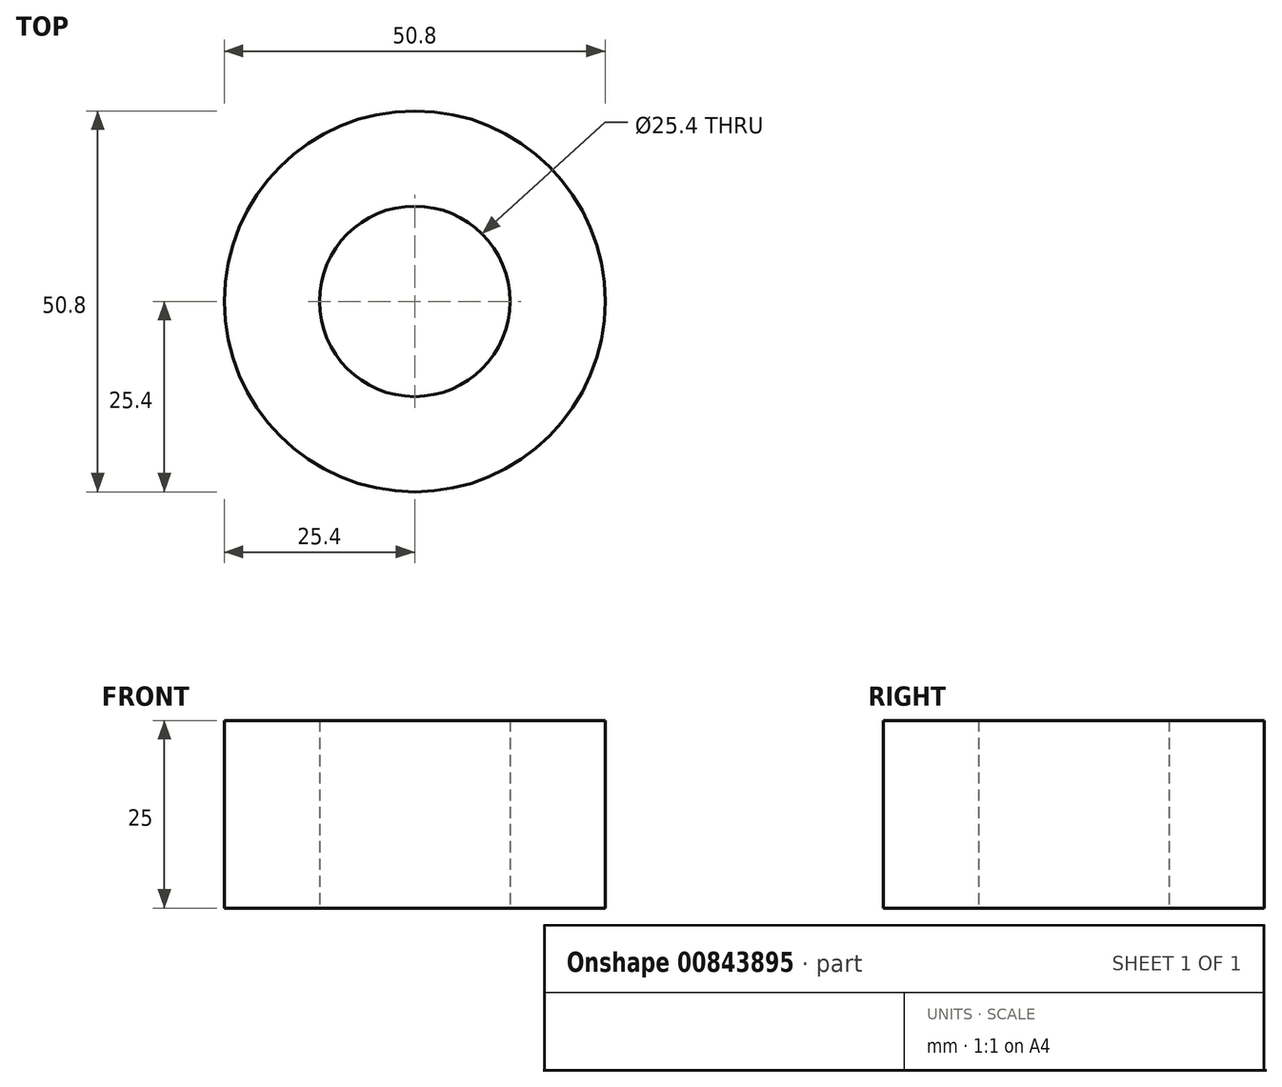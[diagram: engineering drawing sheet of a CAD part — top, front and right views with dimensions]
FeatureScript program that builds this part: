
annotation { "Feature Type Name" : "Feature", "Feature Type Description" : "" }
export const myFeature = defineFeature(function(context is Context, id is Id, definition is map)
    precondition{}
    {
        {
            var Q0;
            Q0=qCreatedBy(makeId("Top.planeOp"),FACE);
            var sketch = newSketch(context, id + "F0", { "sketchPlane" : qUnion([Q0])});
            skCircle(sketch, "E0", {"center": v(0, 0) * mm, "radius": 25.4 * mm});
            skCircle(sketch, "E1", {"center": v(0, 0) * mm, "radius": 12.7 * mm});
            skSolve(sketch);
        }
        {
            var Q0;
            Q0=makeQuery(id+"F0.imprint","IMPRINT",FACE,{"disambiguationData":[TD([[makeQuery(id+"F0.imprint","IMPRINT",EDGE,{"derivedFrom":sQuery(id+"F0.wireOp",EDGE,"E0")}),1.0]])]});
            extrude(context, id + "F1", {"entities" : qUnion([Q0]), "depth" : 25 * mm, "offsetDistance" : 25 * mm});
        }
    });
